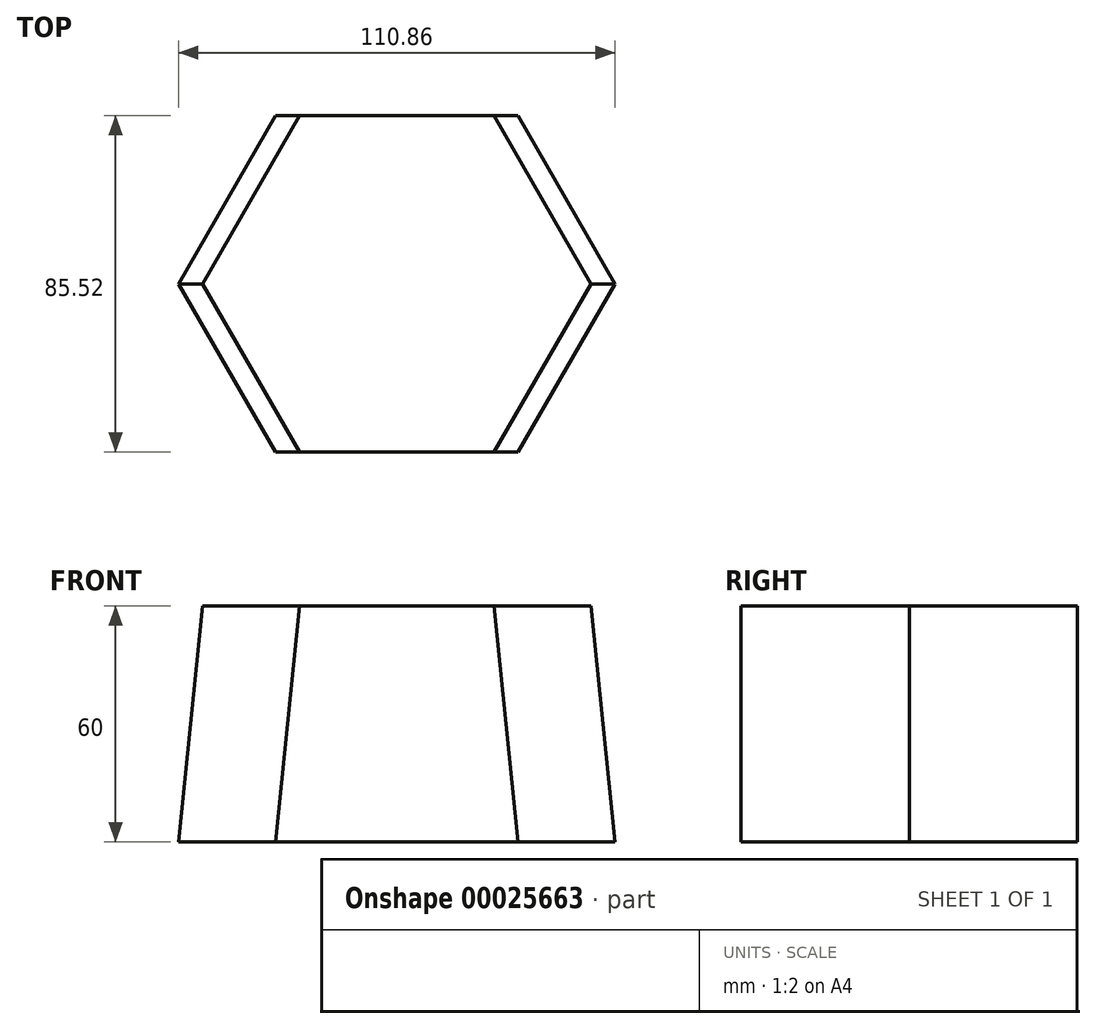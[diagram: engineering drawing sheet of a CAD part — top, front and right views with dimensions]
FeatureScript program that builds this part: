
annotation { "Feature Type Name" : "Feature", "Feature Type Description" : "" }
export const myFeature = defineFeature(function(context is Context, id is Id, definition is map)
    precondition{}
    {
        {
            var Q0;
            Q0=qCreatedBy(makeId("Top.planeOp"),FACE);
            var sketch = newSketch(context, id + "F0", { "sketchPlane" : qUnion([Q0])});
            skLineSegment(sketch, "E0", {"start": v(0, 0) * mm, "end": v(0, 63.67) * mm, "construction": true});
            skLineSegment(sketch, "E1", {"start": v(0, 0) * mm, "end": v(-80.1, 0) * mm, "construction": true});
            skCircle(sketch, "E2.cCircle", {"center": v(0, 0) * mm, "radius": 42.76 * mm, "construction": true});
            skLineSegment(sketch, "E2.0", {"start": v(-24.69, -42.76) * mm, "end": v(-49.37, 0) * mm});
            skLineSegment(sketch, "E2.1", {"start": v(-49.37, 0) * mm, "end": v(-24.69, 42.76) * mm});
            skLineSegment(sketch, "E2.2", {"start": v(-24.69, 42.76) * mm, "end": v(24.69, 42.76) * mm});
            skLineSegment(sketch, "E2.3", {"start": v(24.69, 42.76) * mm, "end": v(49.37, 0) * mm});
            skLineSegment(sketch, "E2.4", {"start": v(49.37, 0) * mm, "end": v(24.69, -42.76) * mm});
            skLineSegment(sketch, "E2.5", {"start": v(24.69, -42.76) * mm, "end": v(-24.69, -42.76) * mm});
            skPoint(sketch, "E2.0.midPoint", {"position": v(-37.03, -21.38) * mm});
            skSolve(sketch);
        }
        {
            var Q0;
            Q0 = qSketchRegion(id + "F0", true);
            extrude(context, id + "F1", {"entities" : qUnion([Q0]), "oppositeDirection" : true, "depth" : 60 * mm, "hasDraft" : true, "draftAngle" : 5 * degree});
        }
        {
            var Q0;
            Q0=qCreatedBy(makeId("Top.planeOp"),FACE);
            var sketch = newSketch(context, id + "F2", { "sketchPlane" : qUnion([Q0])});
            skLineSegment(sketch, "E3.bottom", {"start": v(-60.44, 0) * mm, "end": v(63.4, 0) * mm});
            skLineSegment(sketch, "E3.top", {"start": v(-60.44, -58.56) * mm, "end": v(63.4, -58.56) * mm});
            skLineSegment(sketch, "E3.left", {"start": v(-60.44, 0) * mm, "end": v(-60.44, -58.56) * mm});
            skLineSegment(sketch, "E3.right", {"start": v(63.4, 0) * mm, "end": v(63.4, -58.56) * mm});
            skSolve(sketch);
        }
        {
            var Q0;
            Q0 = qSketchRegion(id + "F2", true);
            extrude(context, id + "F3", {"entities" : qUnion([Q0]), "operationType" : NewBodyOperationType.REMOVE, "oppositeDirection" : true, "depth" : 82 * mm});
        }
        {
            var Q0;
            Q0=makeQuery(id+"F1.opExtrude","CAP_FACE",FACE,{"disambiguationData":[OSD([sQuery(id+"F0.wireOp",EDGE,"E2.0"),sQuery(id+"F0.wireOp",EDGE,"E2.1"),sQuery(id+"F0.wireOp",EDGE,"E2.2"),sQuery(id+"F0.wireOp",EDGE,"E2.3"),sQuery(id+"F0.wireOp",EDGE,"E2.4"),sQuery(id+"F0.wireOp",EDGE,"E2.5")])],"isStart":true});
            var sketch = newSketch(context, id + "F4", { "sketchPlane" : qUnion([Q0])});
            skLineSegment(sketch, "E4", {"start": v(-24.69, 42.76) * mm, "end": v(-49.64, 42.76) * mm, "construction": true});
            skLineSegment(sketch, "E5.bottom", {"start": v(-49.64, 42.76) * mm, "end": v(48.58, 42.76) * mm});
            skLineSegment(sketch, "E5.top", {"start": v(-49.64, 55.02) * mm, "end": v(48.58, 55.02) * mm});
            skLineSegment(sketch, "E5.left", {"start": v(-49.64, 42.76) * mm, "end": v(-49.64, 55.02) * mm});
            skLineSegment(sketch, "E5.right", {"start": v(48.58, 42.76) * mm, "end": v(48.58, 55.02) * mm});
            skSolve(sketch);
        }
        {
            var Q0;
            Q0 = qSketchRegion(id + "F4", true);
            extrude(context, id + "F5", {"entities" : qUnion([Q0]), "operationType" : NewBodyOperationType.REMOVE, "oppositeDirection" : true, "depth" : 78.5 * mm});
        }
        {
            var Q0;
            Q0=makeQuery(id+"F1.opExtrude","SWEPT_BODY",BODY,{"disambiguationData":[OSD([sQuery(id+"F0.wireOp",EDGE,"E2.0"),sQuery(id+"F0.wireOp",EDGE,"E2.1"),sQuery(id+"F0.wireOp",EDGE,"E2.2"),sQuery(id+"F0.wireOp",EDGE,"E2.3"),sQuery(id+"F0.wireOp",EDGE,"E2.4"),sQuery(id+"F0.wireOp",EDGE,"E2.5")])]});
            var Q1;
            Q1=qCreatedBy(makeId("Front.planeOp"),FACE);
            mirror(context, id + "F6", {"operationType" : NewBodyOperationType.ADD, "entities" : qUnion([Q0]), "mirrorPlane" : qUnion([Q1])});
        }
    });
